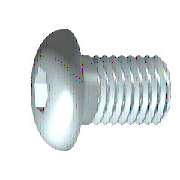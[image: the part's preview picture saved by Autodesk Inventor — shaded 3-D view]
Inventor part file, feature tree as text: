
AUTODESK INVENTOR PART (.ipt)
format: ipt  version: 2023.5 (Build 275446000, 446)  size: 188,928 bytes
history: native  units: mm (DEFAULTED — no unit token found)
features: extrude x1, plane x1, fillet x1
ambient origin geometry x7: Origin, YZ Plane, XY Plane, X Axis, Y Axis, Z Axis, Center Point
bodies: Solid1 (feature_tree), Body (feature_tree)
feature tree (3):
  extrude  "Slot"  Depth=23.3678mm
  plane  "Work Plane1"
  fillet  "Fillet2"  Radius=2.0321mm
